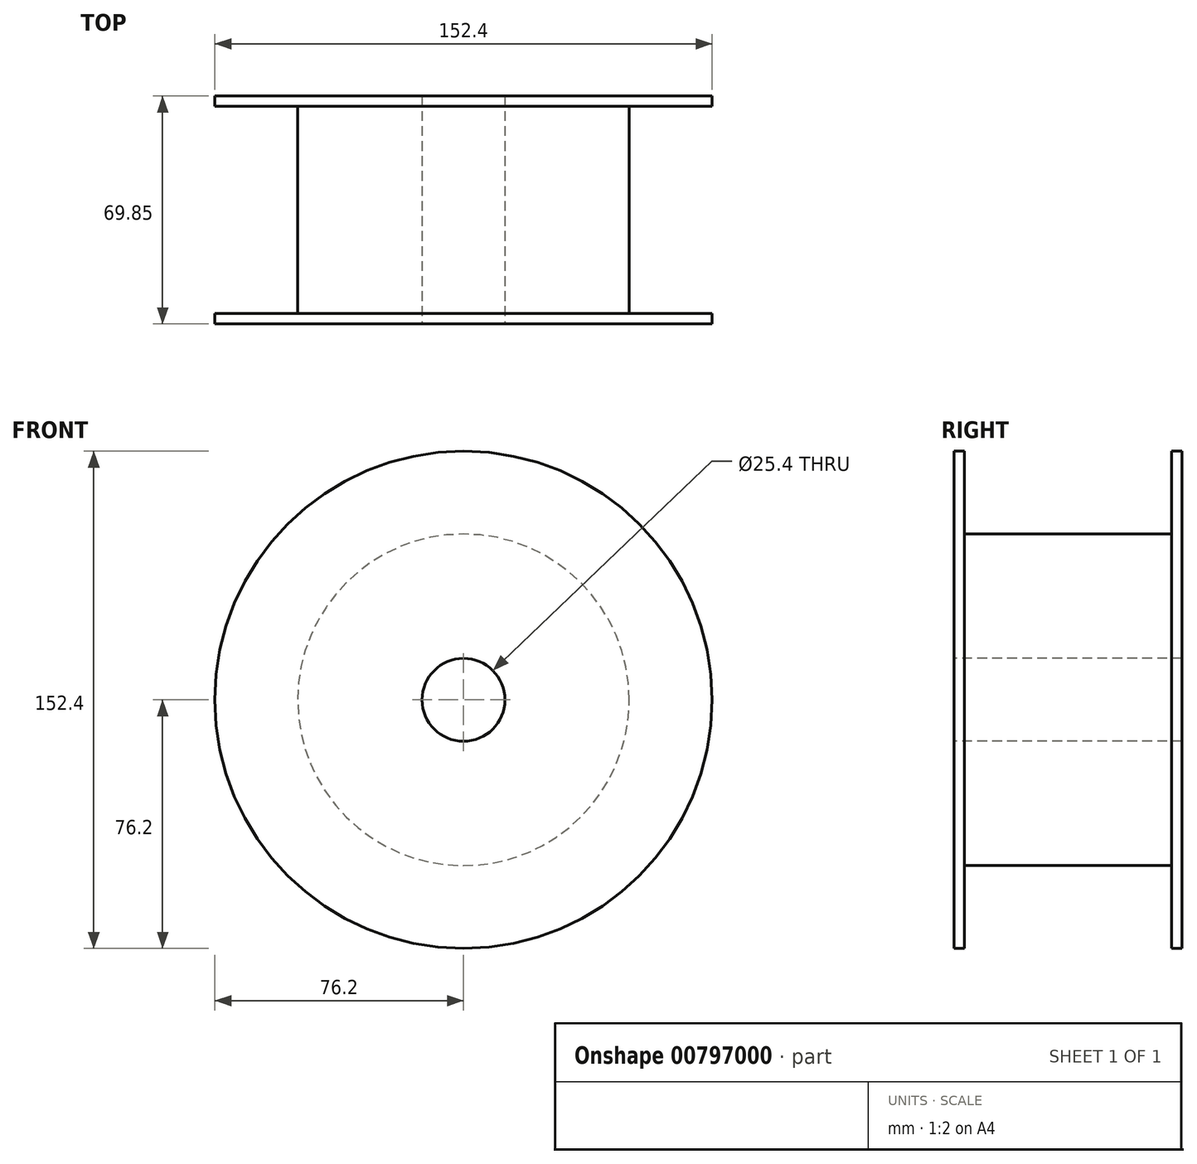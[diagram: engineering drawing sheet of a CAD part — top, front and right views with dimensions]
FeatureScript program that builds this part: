
annotation { "Feature Type Name" : "Feature", "Feature Type Description" : "" }
export const myFeature = defineFeature(function(context is Context, id is Id, definition is map)
    precondition{}
    {
        {
            var Q0;
            Q0=qCreatedBy(makeId("Front.planeOp"),FACE);
            var sketch = newSketch(context, id + "F0", { "sketchPlane" : qUnion([Q0])});
            skCircle(sketch, "E0", {"center": v(0, 0) * mm, "radius": 76.2 * mm});
            skSolve(sketch);
        }
        {
            var Q0;
            Q0=makeQuery(id+"F0.imprint","IMPRINT",FACE,{"disambiguationData":[TD([[makeQuery(id+"F0.imprint","IMPRINT",EDGE,{"derivedFrom":sQuery(id+"F0.wireOp",EDGE,"E0")}),1.0]])]});
            extrude(context, id + "F1", {"entities" : qUnion([Q0]), "depth" : 3.17 * mm, "offsetDistance" : 25.4 * mm});
        }
        {
            var Q0;
            Q0=makeQuery(id+"F1.opExtrude","CAP_FACE",FACE,{"disambiguationData":[OSD([sQuery(id+"F0.wireOp",EDGE,"E0")])],"isStart":false});
            var sketch = newSketch(context, id + "F2", { "sketchPlane" : qUnion([Q0])});
            skCircle(sketch, "E1", {"center": v(0, 0) * mm, "radius": 50.8 * mm});
            skSolve(sketch);
        }
        {
            var Q0;
            Q0 = qSketchRegion(id + "F2", true);
            extrude(context, id + "F3", {"entities" : qUnion([Q0]), "operationType" : NewBodyOperationType.ADD, "depth" : 63.5 * mm, "offsetDistance" : 25.4 * mm});
        }
        {
            var Q0;
            Q0=makeQuery(id+"F3.opExtrude","CAP_FACE",FACE,{"disambiguationData":[OSD([sQuery(id+"F2.wireOp",EDGE,"E1")])],"isStart":false});
            var sketch = newSketch(context, id + "F4", { "sketchPlane" : qUnion([Q0])});
            skCircle(sketch, "E2", {"center": v(0, 0) * mm, "radius": 76.2 * mm});
            skSolve(sketch);
        }
        {
            var Q0;
            Q0 = qSketchRegion(id + "F4", true);
            extrude(context, id + "F5", {"entities" : qUnion([Q0]), "operationType" : NewBodyOperationType.ADD, "depth" : 3.17 * mm, "offsetDistance" : 25.4 * mm});
        }
        {
            var Q0;
            Q0=makeQuery(id+"F5.opExtrude","CAP_FACE",FACE,{"disambiguationData":[OSD([sQuery(id+"F4.wireOp",EDGE,"E2")])],"isStart":false});
            var sketch = newSketch(context, id + "F6", { "sketchPlane" : qUnion([Q0])});
            skCircle(sketch, "E3", {"center": v(0, 0) * mm, "radius": 12.7 * mm});
            skSolve(sketch);
        }
        {
            var Q0;
            Q0 = qSketchRegion(id + "F6", true);
            extrude(context, id + "F7", {"entities" : qUnion([Q0]), "operationType" : NewBodyOperationType.REMOVE, "oppositeDirection" : true, "depth" : 254 * mm, "offsetDistance" : 25.4 * mm});
        }
    });
